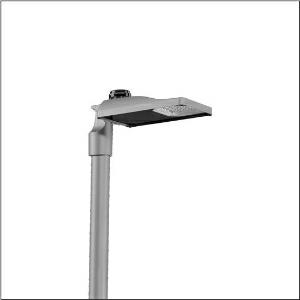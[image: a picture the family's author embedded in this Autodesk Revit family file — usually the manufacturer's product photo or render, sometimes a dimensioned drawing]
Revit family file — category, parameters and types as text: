
# Revit family: streetlight_sl_31_micro___st1_5a_5xh1p7bn08ca_d18d
name_source: partatom
category: Lighting Fixtures
units: mm (PartAtom-declared; Revit-internal decimal feet)

## family parameters
Cut with Voids When Loaded = No
Host = Face
Light Source = No
Part Type = Normal
Room Calculation Point = No
Round Connector Dimension = Use Diameter
Shared = No

## types (1)
- --- (1 x LED, 1150 lm, 10.3 W, 2200K)
    Apparent Load = 10 VA
    CIE Flux Codes = 22 53 95 100 100
    Color Rendering = 70
    Color Temperature = 2200K
    Default Elevation = 1800 mm
    Description = Streetlight SL 31 micro NEMA (7pin) mast luminaire for post-top, side-entry; light control with lens of PMMA; light distribution: ST1.5a, direct asymmetric distribution, for standard-compliant lighting for roads and squares; LED: luminous flux: 1.150lm, light colour: 722, colour temperature: 2200K; luminous efficacy: 111,7lm/W; control: overheat protection, intelligent temperature release in ECG and LED module, constant luminous flux control, time-dependent luminous flux control, flexible luminous flux parameterisation, pre-setting: linear dimming characteristic; luminaire housing, of diecast aluminium, SITECO metallic grey (DB 702S), corrosivity category C5 high according to DIN EN ISO 12944; cover of toughened safety glass, transparent, mast flange of diecast aluminium, SITECO metallic grey (DB 702S), spigot size: 76/60mm, mast flange included unmounted; cable length: 5,5m, connection cable pre-assembled; mains connection: 220..240V, AC, 50/60Hz; power consumption (at start of service life): 10,3W / (at end of service life): 10,6W / (with reduced operation 50%): 5,3W; protection rating (complete): IP66; insulation class (complete): insulation class I (protective earthing); impact resistance: IK10; certification: CE, ENEC, ENEC+, VDE, UKCA; permissible operating ambient temperature for outdoor applications: -40..+50°C; packaging unit: 1 piece

Light Distribution: ST1.5a
    Height = 76 mm
    Lamp = 1 x LED
    Lamp Light Flux = 1150 lm
    Lamp Power = 10.3 W
    Lamp count = 1
    Length = 467 mm
    Luminous efficacy = 112 lm/W
    Manufacturer = Siteco
    ModVariant = No
    Model = 5XH1P7BN08CA
    Number of Poles = 1
    OnlyDefault = Yes
    Power Factor = 1
    Product Name = Streetlight SL 31 micro | ST1.5a
    Product group = mast luminaire | pylon top
    ProductGroupID = 6100
    Protection Class = Protection class I
    Protection Degree = IP 66
    RLX_Detail_Level = 1
    RLX_Emergency_Light_Flux = 0 lm
    RLX_Emergency_Type = 0
    RLX_Emergency_Type_DB = No
    RlxData = <blob elided: 26349 chars, md5=01ad9738>
    Socket = socket
    Standby Power = 0 W
    System Light Flux = 1150 lm
    System Power = 10 W
    Type Comments = factory setting: luminous flux: 100 % | dim-lin: 254 | 386 mA
    Type Image = l_1300305.jpg
    URL = http://relux.com
    VarID = @adj_009849
    Voltage = 0 V
    Weight = 0.00 kg
    Width = 265 mm

## geometry (parser evidence)
native form markers: Blend x4, Sweep x12
no freeform markers — native parametric forms only
